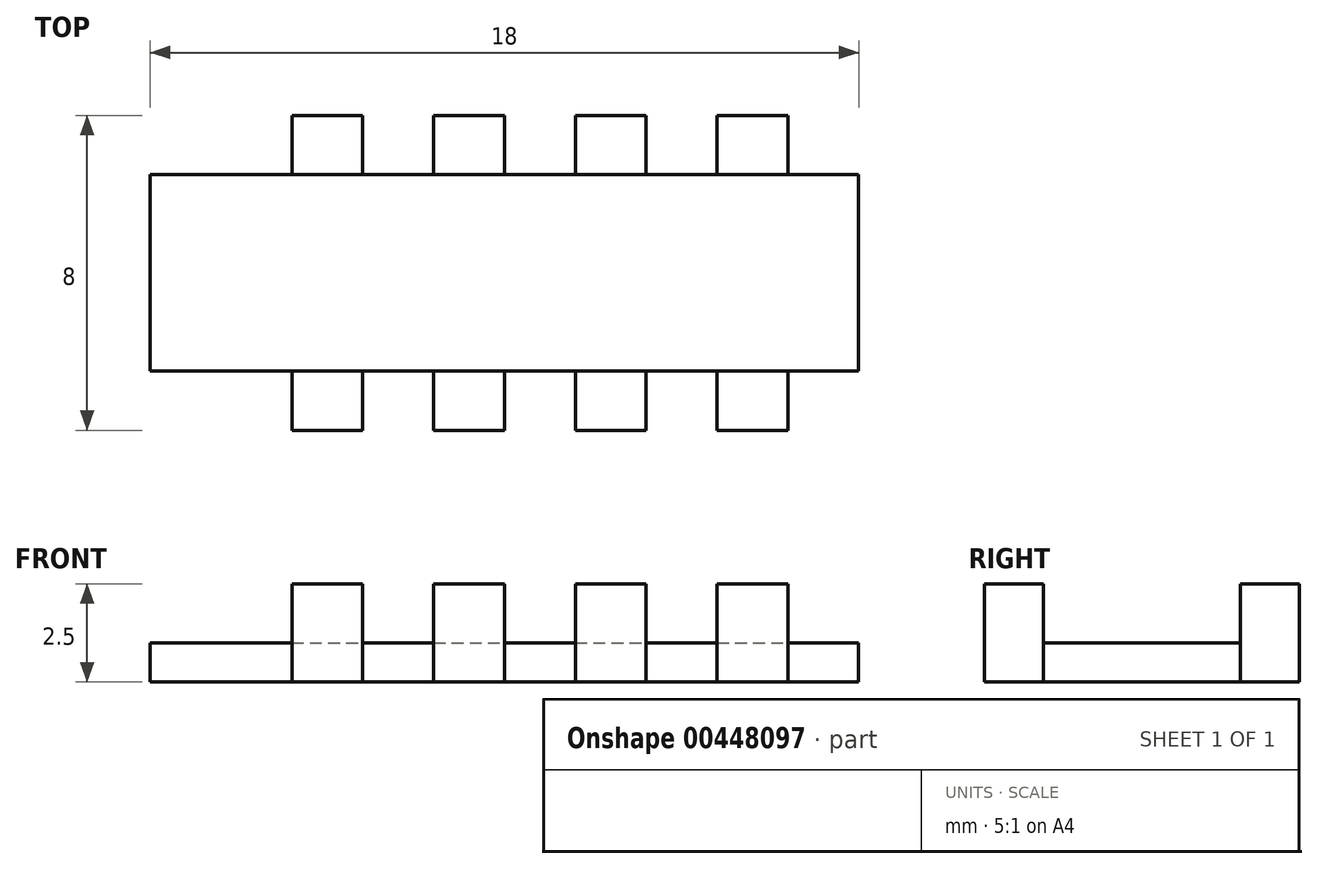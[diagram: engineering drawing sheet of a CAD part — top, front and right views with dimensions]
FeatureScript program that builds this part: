
annotation { "Feature Type Name" : "Feature", "Feature Type Description" : "" }
export const myFeature = defineFeature(function(context is Context, id is Id, definition is map)
    precondition{}
    {
        {
            var Q0;
            Q0=qCreatedBy(makeId("Top.planeOp"),FACE);
            var sketch = newSketch(context, id + "F0", { "sketchPlane" : qUnion([Q0])});
            skLineSegment(sketch, "E0.bottom", {"start": v(-21.28, 0.96) * mm, "end": v(-3.28, 0.96) * mm});
            skLineSegment(sketch, "E0.left", {"start": v(-21.28, 0.96) * mm, "end": v(-21.28, -3.04) * mm});
            skLineSegment(sketch, "E0.right", {"start": v(-3.28, 0.96) * mm, "end": v(-3.28, -3.04) * mm});
            skLineSegment(sketch, "E1.bottom", {"start": v(-21.28, 0.96) * mm, "end": v(-19.48, 0.96) * mm});
            skLineSegment(sketch, "E1.top", {"start": v(-21.28, 2.46) * mm, "end": v(-19.48, 2.46) * mm});
            skLineSegment(sketch, "E1.left", {"start": v(-21.28, 0.96) * mm, "end": v(-21.28, 2.46) * mm});
            skLineSegment(sketch, "E1.right", {"start": v(-19.48, 0.96) * mm, "end": v(-19.48, 2.46) * mm});
            skLineSegment(sketch, "E2.bottom", {"start": v(-19.48, 2.46) * mm, "end": v(-17.68, 2.46) * mm});
            skLineSegment(sketch, "E2.top", {"start": v(-19.48, 0.96) * mm, "end": v(-17.68, 0.96) * mm});
            skLineSegment(sketch, "E2.left", {"start": v(-19.48, 2.46) * mm, "end": v(-19.48, 0.96) * mm});
            skLineSegment(sketch, "E2.right", {"start": v(-17.68, 2.46) * mm, "end": v(-17.68, 0.96) * mm});
            skLineSegment(sketch, "E3.bottom", {"start": v(-17.68, 2.46) * mm, "end": v(-15.88, 2.46) * mm});
            skLineSegment(sketch, "E3.top", {"start": v(-17.68, 0.96) * mm, "end": v(-15.88, 0.96) * mm});
            skLineSegment(sketch, "E3.right", {"start": v(-15.88, 2.46) * mm, "end": v(-15.88, 0.96) * mm});
            skLineSegment(sketch, "E4.bottom", {"start": v(-15.88, 2.46) * mm, "end": v(-14.08, 2.46) * mm});
            skLineSegment(sketch, "E4.top", {"start": v(-15.88, 0.96) * mm, "end": v(-14.08, 0.96) * mm});
            skLineSegment(sketch, "E4.right", {"start": v(-14.08, 2.46) * mm, "end": v(-14.08, 0.96) * mm});
            skLineSegment(sketch, "E5.bottom", {"start": v(-14.08, 2.46) * mm, "end": v(-12.28, 2.46) * mm});
            skLineSegment(sketch, "E5.top", {"start": v(-14.08, 0.96) * mm, "end": v(-12.28, 0.96) * mm});
            skLineSegment(sketch, "E5.right", {"start": v(-12.28, 2.46) * mm, "end": v(-12.28, 0.96) * mm});
            skLineSegment(sketch, "E6.bottom", {"start": v(-12.28, 2.46) * mm, "end": v(-10.48, 2.46) * mm});
            skLineSegment(sketch, "E6.top", {"start": v(-12.28, 0.96) * mm, "end": v(-10.48, 0.96) * mm});
            skLineSegment(sketch, "E6.right", {"start": v(-10.48, 2.46) * mm, "end": v(-10.48, 0.96) * mm});
            skLineSegment(sketch, "E7.bottom", {"start": v(-10.48, 2.46) * mm, "end": v(-8.68, 2.46) * mm});
            skLineSegment(sketch, "E7.top", {"start": v(-10.48, 0.96) * mm, "end": v(-8.68, 0.96) * mm});
            skLineSegment(sketch, "E7.right", {"start": v(-8.68, 2.46) * mm, "end": v(-8.68, 0.96) * mm});
            skLineSegment(sketch, "E8.bottom", {"start": v(-8.68, 2.46) * mm, "end": v(-6.88, 2.46) * mm});
            skLineSegment(sketch, "E8.top", {"start": v(-8.68, 0.96) * mm, "end": v(-6.88, 0.96) * mm});
            skLineSegment(sketch, "E8.right", {"start": v(-6.88, 2.46) * mm, "end": v(-6.88, 0.96) * mm});
            skLineSegment(sketch, "E9.bottom", {"start": v(-6.88, 2.46) * mm, "end": v(-5.08, 2.46) * mm});
            skLineSegment(sketch, "E9.top", {"start": v(-6.88, 0.96) * mm, "end": v(-5.08, 0.96) * mm});
            skLineSegment(sketch, "E9.right", {"start": v(-5.08, 2.46) * mm, "end": v(-5.08, 0.96) * mm});
            skLineSegment(sketch, "E10.bottom", {"start": v(-5.08, 2.46) * mm, "end": v(-3.28, 2.46) * mm});
            skLineSegment(sketch, "E10.top", {"start": v(-5.08, 0.96) * mm, "end": v(-3.28, 0.96) * mm});
            skLineSegment(sketch, "E10.right", {"start": v(-3.28, 2.46) * mm, "end": v(-3.28, 0.96) * mm});
            skLineSegment(sketch, "E11.MirrorCS", {"start": v(-8.68, -5.54) * mm, "end": v(-8.68, -4.04) * mm});
            skLineSegment(sketch, "E12.MirrorCS", {"start": v(-10.48, -5.54) * mm, "end": v(-10.48, -4.04) * mm});
            skLineSegment(sketch, "E13.MirrorCS", {"start": v(-19.48, -4.04) * mm, "end": v(-19.48, -5.54) * mm});
            skLineSegment(sketch, "E14.MirrorCS", {"start": v(-15.88, -5.54) * mm, "end": v(-15.88, -4.04) * mm});
            skLineSegment(sketch, "E15.MirrorCS", {"start": v(-17.68, -5.54) * mm, "end": v(-17.68, -4.04) * mm});
            skLineSegment(sketch, "E16.MirrorCS", {"start": v(-17.68, -4.04) * mm, "end": v(-15.88, -4.04) * mm});
            skLineSegment(sketch, "E17.MirrorCS", {"start": v(-6.88, -5.54) * mm, "end": v(-6.88, -4.04) * mm});
            skLineSegment(sketch, "E18.MirrorCS", {"start": v(-14.08, -5.54) * mm, "end": v(-14.08, -4.04) * mm});
            skLineSegment(sketch, "E19.MirrorCS", {"start": v(-12.28, -5.54) * mm, "end": v(-12.28, -4.04) * mm});
            skLineSegment(sketch, "E20.MirrorCS", {"start": v(-5.08, -5.54) * mm, "end": v(-5.08, -4.04) * mm});
            skLineSegment(sketch, "E21.MirrorCS", {"start": v(-8.68, -5.54) * mm, "end": v(-6.88, -5.54) * mm});
            skLineSegment(sketch, "E22.MirrorCS", {"start": v(-15.88, -5.54) * mm, "end": v(-14.08, -5.54) * mm});
            skLineSegment(sketch, "E23.MirrorCS", {"start": v(-10.48, -4.04) * mm, "end": v(-8.68, -4.04) * mm});
            skLineSegment(sketch, "E24.MirrorCS", {"start": v(-6.88, -5.54) * mm, "end": v(-5.08, -5.54) * mm});
            skLineSegment(sketch, "E25.MirrorCS", {"start": v(-14.08, -5.54) * mm, "end": v(-12.28, -5.54) * mm});
            skLineSegment(sketch, "E26.MirrorCS", {"start": v(-12.28, -4.04) * mm, "end": v(-10.48, -4.04) * mm});
            skLineSegment(sketch, "E27.MirrorCS", {"start": v(-5.08, -4.04) * mm, "end": v(-3.28, -4.04) * mm});
            skLineSegment(sketch, "E28.MirrorCS", {"start": v(-3.28, -5.54) * mm, "end": v(-3.28, -4.04) * mm});
            skLineSegment(sketch, "E29.MirrorCS", {"start": v(-17.68, -5.54) * mm, "end": v(-15.88, -5.54) * mm});
            skLineSegment(sketch, "E30.MirrorCS", {"start": v(-19.48, -5.54) * mm, "end": v(-19.48, -4.04) * mm});
            skLineSegment(sketch, "E31.MirrorCS", {"start": v(-19.48, -4.04) * mm, "end": v(-17.68, -4.04) * mm});
            skLineSegment(sketch, "E32.MirrorCS", {"start": v(-19.48, -5.54) * mm, "end": v(-17.68, -5.54) * mm});
            skLineSegment(sketch, "E33.MirrorCS", {"start": v(-21.28, -4.04) * mm, "end": v(-21.28, -5.54) * mm});
            skLineSegment(sketch, "E34.MirrorCS", {"start": v(-21.28, -5.54) * mm, "end": v(-19.48, -5.54) * mm});
            skLineSegment(sketch, "E35.MirrorCS", {"start": v(-21.28, -4.04) * mm, "end": v(-19.48, -4.04) * mm});
            skLineSegment(sketch, "E36.MirrorCS", {"start": v(-3.28, -4.04) * mm, "end": v(-3.28, -0.04) * mm});
            skLineSegment(sketch, "E37.MirrorCS", {"start": v(-21.28, -4.04) * mm, "end": v(-21.28, -0.04) * mm});
            skLineSegment(sketch, "E38.MirrorCS", {"start": v(-21.28, -4.04) * mm, "end": v(-3.28, -4.04) * mm});
            skLineSegment(sketch, "E39.MirrorCS", {"start": v(-8.68, -4.04) * mm, "end": v(-6.88, -4.04) * mm});
            skLineSegment(sketch, "E40.MirrorCS", {"start": v(-15.88, -4.04) * mm, "end": v(-14.08, -4.04) * mm});
            skLineSegment(sketch, "E41.MirrorCS", {"start": v(-6.88, -4.04) * mm, "end": v(-5.08, -4.04) * mm});
            skLineSegment(sketch, "E42.MirrorCS", {"start": v(-14.08, -4.04) * mm, "end": v(-12.28, -4.04) * mm});
            skLineSegment(sketch, "E43.MirrorCS", {"start": v(-12.28, -5.54) * mm, "end": v(-10.48, -5.54) * mm});
            skLineSegment(sketch, "E44.MirrorCS", {"start": v(-5.08, -5.54) * mm, "end": v(-3.28, -5.54) * mm});
            skLineSegment(sketch, "E45.MirrorCS", {"start": v(-10.48, -5.54) * mm, "end": v(-8.68, -5.54) * mm});
            skSolve(sketch);
        }
        {
            var Q0;
            {var subQ9=sQuery(id+"F0.wireOp",EDGE,"E0.left");Q0=makeQuery(id+"F0.imprint","IMPRINT",FACE,{"disambiguationData":[TD([[makeQuery(id+"F0.imprint","IMPRINT",EDGE,{"derivedFrom":subQ9}),1.0]])]});}
            extrude(context, id + "F1", {"entities" : qUnion([Q0]), "depth" : 1 * mm});
        }
        {
            var Q0;
            Q0=makeQuery(id+"F0.imprint","IMPRINT",FACE,{"disambiguationData":[TD([[makeQuery(id+"F0.imprint","IMPRINT",EDGE,{"derivedFrom":sQuery(id+"F0.wireOp",EDGE,"E1.bottom")}),1.0]])]});
            var Q1;
            Q1=makeQuery(id+"F0.imprint","IMPRINT",FACE,{"disambiguationData":[TD([[makeQuery(id+"F0.imprint","IMPRINT",EDGE,{"derivedFrom":sQuery(id+"F0.wireOp",EDGE,"E3.bottom")}),-1.0]])]});
            var Q2;
            Q2=makeQuery(id+"F0.imprint","IMPRINT",FACE,{"disambiguationData":[TD([[makeQuery(id+"F0.imprint","IMPRINT",EDGE,{"derivedFrom":sQuery(id+"F0.wireOp",EDGE,"E5.bottom")}),-1.0]])]});
            var Q3;
            Q3=makeQuery(id+"F0.imprint","IMPRINT",FACE,{"disambiguationData":[TD([[makeQuery(id+"F0.imprint","IMPRINT",EDGE,{"derivedFrom":sQuery(id+"F0.wireOp",EDGE,"E7.bottom")}),-1.0]])]});
            var Q4;
            Q4=makeQuery(id+"F0.imprint","IMPRINT",FACE,{"disambiguationData":[TD([[makeQuery(id+"F0.imprint","IMPRINT",EDGE,{"derivedFrom":sQuery(id+"F0.wireOp",EDGE,"E9.bottom")}),-1.0]])]});
            var Q5;
            Q5=makeQuery(id+"F0.imprint","IMPRINT",FACE,{"disambiguationData":[TD([[makeQuery(id+"F0.imprint","IMPRINT",EDGE,{"derivedFrom":sQuery(id+"F0.wireOp",EDGE,"E24.MirrorCS")}),1.0]])]});
            var Q6;
            {var subQ0=sQuery(id+"F0.wireOp",EDGE,"E11.MirrorCS");Q6=makeQuery(id+"F0.imprint","IMPRINT",FACE,{"disambiguationData":[TD([[makeQuery(id+"F0.imprint","IMPRINT",EDGE,{"derivedFrom":subQ0}),1.0]])]});}
            var Q7;
            Q7=makeQuery(id+"F0.imprint","IMPRINT",FACE,{"disambiguationData":[TD([[makeQuery(id+"F0.imprint","IMPRINT",EDGE,{"derivedFrom":sQuery(id+"F0.wireOp",EDGE,"E25.MirrorCS")}),1.0]])]});
            var Q8;
            {var subQ0=sQuery(id+"F0.wireOp",EDGE,"E14.MirrorCS");Q8=makeQuery(id+"F0.imprint","IMPRINT",FACE,{"disambiguationData":[TD([[makeQuery(id+"F0.imprint","IMPRINT",EDGE,{"derivedFrom":subQ0}),1.0]])]});}
            var Q9;
            {var subQ0=sQuery(id+"F0.wireOp",EDGE,"E30.MirrorCS");Q9=makeQuery(id+"F0.imprint","IMPRINT",FACE,{"disambiguationData":[TD([[makeQuery(id+"F0.imprint","IMPRINT",EDGE,{"derivedFrom":subQ0}),1.0]])]});}
            extrude(context, id + "F2", {"entities" : qUnion([Q0, Q1, Q2, Q3, Q4, Q5, Q6, Q7, Q8, Q9]), "operationType" : NewBodyOperationType.ADD, "depth" : 2.5 * mm});
        }
    });
